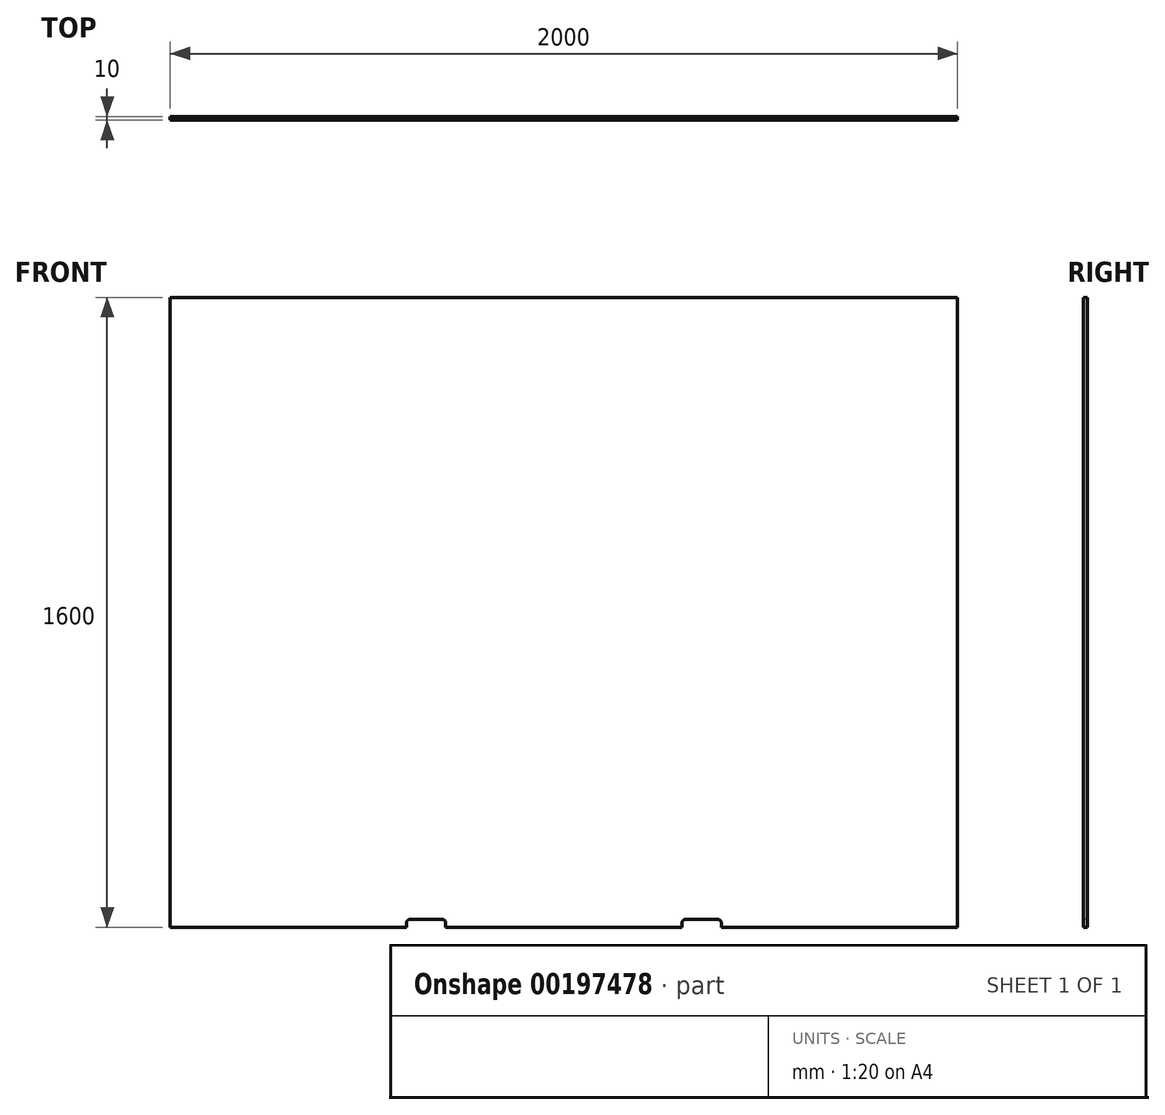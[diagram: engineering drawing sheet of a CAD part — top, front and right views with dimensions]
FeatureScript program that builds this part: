
annotation { "Feature Type Name" : "Feature", "Feature Type Description" : "" }
export const myFeature = defineFeature(function(context is Context, id is Id, definition is map)
    precondition{}
    {
        {
            var Q0;
            Q0=qCreatedBy(makeId("Front.planeOp"),FACE);
            var sketch = newSketch(context, id + "F0", { "sketchPlane" : qUnion([Q0])});
            skLineSegment(sketch, "E0.bottom", {"start": v(1000, 800) * mm, "end": v(-1000, 800) * mm});
            skLineSegment(sketch, "E0.top", {"start": v(1000, -800) * mm, "end": v(-1000, -800) * mm});
            skLineSegment(sketch, "E0.left", {"start": v(1000, 800) * mm, "end": v(1000, -800) * mm});
            skLineSegment(sketch, "E0.right", {"start": v(-1000, 800) * mm, "end": v(-1000, -800) * mm});
            skPoint(sketch, "E0.middle", {"position": v(0, 0) * mm});
            skSolve(sketch);
        }
        {
            var Q0;
            Q0 = qSketchRegion(id + "F0", true);
            extrude(context, id + "F1", {"entities" : qUnion([Q0]), "depth" : 10 * mm});
        }
        {
            var Q0;
            Q0=makeQuery(id+"F1.opExtrude","CAP_FACE",FACE,{"disambiguationData":[OSD([sQuery(id+"F0.wireOp",EDGE,"E0.bottom"),sQuery(id+"F0.wireOp",EDGE,"E0.top"),sQuery(id+"F0.wireOp",EDGE,"E0.left"),sQuery(id+"F0.wireOp",EDGE,"E0.right")])],"isStart":false});
            var sketch = newSketch(context, id + "F2", { "sketchPlane" : qUnion([Q0])});
            skLineSegment(sketch, "E1.bottom", {"start": v(-400, -800) * mm, "end": v(-300, -800) * mm});
            skLineSegment(sketch, "E1.top", {"start": v(-390, -780) * mm, "end": v(-310, -780) * mm});
            skLineSegment(sketch, "E1.left", {"start": v(-400, -800) * mm, "end": v(-400, -790) * mm});
            skLineSegment(sketch, "E1.right", {"start": v(-300, -800) * mm, "end": v(-300, -790) * mm});
            skLineSegment(sketch, "E2.bottom", {"start": v(300, -800) * mm, "end": v(400, -800) * mm});
            skLineSegment(sketch, "E2.top", {"start": v(310, -780) * mm, "end": v(390, -780) * mm});
            skLineSegment(sketch, "E2.left", {"start": v(300, -800) * mm, "end": v(300, -790) * mm});
            skLineSegment(sketch, "E2.right", {"start": v(400, -800) * mm, "end": v(400, -790) * mm});
            skPoint(sketch, "E3.visualSharp", {"position": v(-400, -780) * mm});
            skArc(sketch, "E3.filletArc", {"start": v(-390, -780) * mm, "mid": v(-397.07, -782.93) * mm, "end": v(-400, -790) * mm});
            skPoint(sketch, "E4.visualSharp", {"position": v(-300, -780) * mm});
            skArc(sketch, "E4.filletArc", {"start": v(-300, -790) * mm, "mid": v(-302.93, -782.93) * mm, "end": v(-310, -780) * mm});
            skPoint(sketch, "E5.visualSharp", {"position": v(300, -780) * mm});
            skArc(sketch, "E5.filletArc", {"start": v(310, -780) * mm, "mid": v(302.93, -782.93) * mm, "end": v(300, -790) * mm});
            skPoint(sketch, "E6.visualSharp", {"position": v(400, -780) * mm});
            skArc(sketch, "E6.filletArc", {"start": v(400, -790) * mm, "mid": v(397.07, -782.93) * mm, "end": v(390, -780) * mm});
            skSolve(sketch);
        }
        {
            var Q0;
            Q0 = qSketchRegion(id + "F2", true);
            extrude(context, id + "F3", {"entities" : qUnion([Q0]), "operationType" : NewBodyOperationType.REMOVE, "oppositeDirection" : true, "depth" : 18 * mm});
        }
    });
